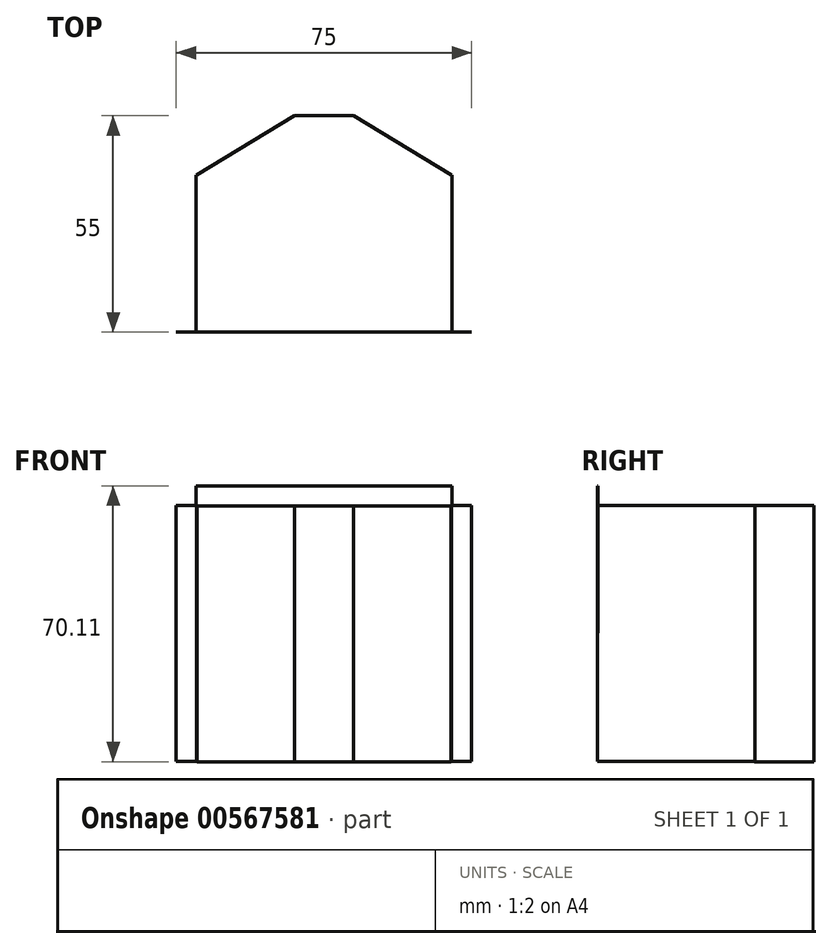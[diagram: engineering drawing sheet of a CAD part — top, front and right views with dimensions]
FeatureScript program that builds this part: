
annotation { "Feature Type Name" : "Feature", "Feature Type Description" : "" }
export const myFeature = defineFeature(function(context is Context, id is Id, definition is map)
    precondition{}
    {
        {
            var Q0;
            Q0=qCreatedBy(makeId("Front.planeOp"),FACE);
            var sketch = newSketch(context, id + "F0", { "sketchPlane" : qUnion([Q0])});
            skLineSegment(sketch, "E0", {"start": v(0, 0) * mm, "end": v(-65, 0) * mm});
            skLineSegment(sketch, "E1", {"start": v(-65, 0) * mm, "end": v(-65, -65) * mm});
            skLineSegment(sketch, "E2", {"start": v(-65, -65) * mm, "end": v(-64.89, -65) * mm});
            skLineSegment(sketch, "E3", {"start": v(-64.89, -65) * mm, "end": v(-64.89, -0.11) * mm});
            skLineSegment(sketch, "E4", {"start": v(-64.89, -0.1) * mm, "end": v(-0.11, -0.1) * mm});
            skLineSegment(sketch, "E5", {"start": v(-0.11, -0.1) * mm, "end": v(-0.1, -65) * mm});
            skLineSegment(sketch, "E6", {"start": v(-0.1, -65) * mm, "end": v(0, -65) * mm});
            skLineSegment(sketch, "E7", {"start": v(0, -65) * mm, "end": v(0, 0) * mm});
            skSolve(sketch);
        }
        {
            var Q0;
            Q0=makeQuery(id+"F0.imprint","IMPRINT",FACE,{"disambiguationData":[TD([[makeQuery(id+"F0.imprint","IMPRINT",EDGE,{"derivedFrom":sQuery(id+"F0.wireOp",EDGE,"E0")}),1.0]])]});
            extrude(context, id + "F1", {"entities" : qUnion([Q0]), "depth" : 35 * mm, "offsetDistance" : 25 * mm});
        }
        {
            var Q0;
            Q0=makeQuery(id+"F1.opExtrude","SWEPT_FACE",FACE,{"disambiguationData":[OSD([sQuery(id+"F0.wireOp",EDGE,"E1")])]});
            var sketch = newSketch(context, id + "F2", { "sketchPlane" : qUnion([Q0])});
            skLineSegment(sketch, "E8", {"start": v(34.9, 0) * mm, "end": v(34.9, -65) * mm});
            skSolve(sketch);
        }
        {
            var Q0;
            {var subQ0=sQuery(id+"F2.wireOp",EDGE,"E8");Q0=makeQuery(id+"F2.imprint","IMPRINT",FACE,{"disambiguationData":[TD([[makeQuery(id+"F2.imprint","IMPRINT",EDGE,{"derivedFrom":subQ0}),1.0]])]});}
            extrude(context, id + "F3", {"entities" : qUnion([Q0]), "operationType" : NewBodyOperationType.ADD, "depth" : 5 * mm, "offsetDistance" : 25 * mm});
        }
        {
            var Q0;
            {var subQ0=sQuery(id+"F0.wireOp",EDGE,"E0");Q0=makeQuery(id+"F3.boolean.opBoolean","MERGE",FACE,{"derivedFrom":[makeQuery(id+"Fdze2Mgvsd4NKJJ_1.boolean.opBoolean","MERGE",FACE,{"derivedFrom":[makeQuery(id+"F1.opExtrude","SWEPT_FACE",FACE,{"disambiguationData":[OSD([subQ0])]}),makeQuery(id+"Fdze2Mgvsd4NKJJ_1.opExtrude","SWEPT_FACE",FACE,{"disambiguationData":[OSD([sQuery(id+"FzqWdQqcZOJAViu_1.wireOp",EDGE,"lwhyzzlY-dMcn-4o8W-08A6-9XrshBXt5lzN.bottom")])]})]}),makeQuery(id+"F3.opExtrude","SWEPT_FACE",FACE,{"disambiguationData":[OSD([subQ0,sQuery(id+"F0.wireOp",EDGE,"E1")])]})]});}
            var sketch = newSketch(context, id + "F4", { "sketchPlane" : qUnion([Q0])});
            skLineSegment(sketch, "E9", {"start": v(-65, -34.9) * mm, "end": v(0, -35) * mm});
            skLineSegment(sketch, "E10", {"start": v(-65, -34.9) * mm, "end": v(-65, -35) * mm});
            skSolve(sketch);
        }
        {
            var Q0;
            {var subQ0=sQuery(id+"F4.wireOp",EDGE,"E9");Q0=makeQuery(id+"F4.imprint","IMPRINT",FACE,{"disambiguationData":[TD([[makeQuery(id+"F4.imprint","IMPRINT",EDGE,{"derivedFrom":subQ0}),-1.0]])]});}
            extrude(context, id + "F5", {"entities" : qUnion([Q0]), "operationType" : NewBodyOperationType.ADD, "depth" : 5 * mm, "offsetDistance" : 25 * mm});
        }
        {
            var Q0;
            Q0=makeQuery(id+"Fdze2Mgvsd4NKJJ_1.boolean.opBoolean","MERGE",FACE,{"derivedFrom":[makeQuery(id+"F1.opExtrude","SWEPT_FACE",FACE,{"disambiguationData":[OSD([sQuery(id+"F0.wireOp",EDGE,"E7")])]}),makeQuery(id+"Fdze2Mgvsd4NKJJ_1.opExtrude","SWEPT_FACE",FACE,{"disambiguationData":[OSD([sQuery(id+"FzqWdQqcZOJAViu_1.wireOp",EDGE,"lwhyzzlY-dMcn-4o8W-08A6-9XrshBXt5lzN.right")])]})]});
            var sketch = newSketch(context, id + "F6", { "sketchPlane" : qUnion([Q0])});
            skLineSegment(sketch, "E11", {"start": v(-34.89, 0) * mm, "end": v(-35, -65) * mm});
            skSolve(sketch);
        }
        {
            var Q0;
            {var subQ0=sQuery(id+"F6.wireOp",EDGE,"E11");Q0=makeQuery(id+"F6.imprint","IMPRINT",FACE,{"disambiguationData":[TD([[makeQuery(id+"F6.imprint","IMPRINT",EDGE,{"derivedFrom":subQ0}),-1.0]])]});}
            extrude(context, id + "F7", {"entities" : qUnion([Q0]), "operationType" : NewBodyOperationType.ADD, "depth" : 5 * mm, "offsetDistance" : 25 * mm});
        }
        {
            var Q0;
            Q0=makeQuery(id+"F1.opExtrude","CAP_FACE",FACE,{"disambiguationData":[OSD([sQuery(id+"F0.wireOp",EDGE,"E0"),sQuery(id+"F0.wireOp",EDGE,"E1"),sQuery(id+"F0.wireOp",EDGE,"E2"),sQuery(id+"F0.wireOp",EDGE,"E3"),sQuery(id+"F0.wireOp",EDGE,"E4"),sQuery(id+"F0.wireOp",EDGE,"E5"),sQuery(id+"F0.wireOp",EDGE,"E6"),sQuery(id+"F0.wireOp",EDGE,"E7")])],"isStart":true});
            extrude(context, id + "F8", {"entities" : qUnion([Q0]), "operationType" : NewBodyOperationType.ADD, "depth" : 20 * mm, "offsetDistance" : 25 * mm});
        }
        {
            var Q0;
            {var subQ0=sQuery(id+"F0.wireOp",EDGE,"E0");var subQ1=sQuery(id+"F0.wireOp",EDGE,"E7");var subQ2=sQuery(id+"F0.wireOp",EDGE,"E1");var subQ3=makeQuery(id+"F3.opExtrude","SWEPT_FACE",FACE,{"disambiguationData":[OSD([subQ0,subQ2])]});var subQ4=makeQuery(id+"F1.opExtrude","SWEPT_FACE",FACE,{"disambiguationData":[OSD([subQ0])]});Q0=makeQuery(id+"F8.boolean.opBoolean","MERGE",FACE,{"derivedFrom":[makeQuery(id+"F7.boolean.opBoolean","MERGE",FACE,{"derivedFrom":[makeQuery(id+"F5.boolean.opBoolean","SPLIT",FACE,{"disambiguationData":[TD([makeQuery(id+"F1.opExtrude","SWEPT_FACE",FACE,{"disambiguationData":[OSD([subQ1])]})])],"derivedFrom":makeQuery(id+"F3.boolean.opBoolean","MERGE",FACE,{"derivedFrom":[subQ4,subQ3]})}),makeQuery(id+"F7.opExtrude","SWEPT_FACE",FACE,{"disambiguationData":[OSD([subQ0,subQ1])]})]}),makeQuery(id+"F8.opExtrude","SWEPT_FACE",FACE,{"disambiguationData":[OSD([subQ0])]})]});}
            var sketch = newSketch(context, id + "F9", { "sketchPlane" : qUnion([Q0])});
            skLineSegment(sketch, "E12", {"start": v(-40, 20) * mm, "end": v(-25, 20) * mm});
            skLineSegment(sketch, "E13", {"start": v(-25, 20) * mm, "end": v(-0.1, 5) * mm});
            skLineSegment(sketch, "E14", {"start": v(-0.11, 5) * mm, "end": v(0, 5) * mm});
            skLineSegment(sketch, "E15", {"start": v(-40, 20) * mm, "end": v(-64.89, 5) * mm});
            skLineSegment(sketch, "E16", {"start": v(-64.89, 5) * mm, "end": v(-65, 5) * mm});
            skSolve(sketch);
        }
        {
            var Q0;
            {var subQ0=sQuery(id+"F9.wireOp",EDGE,"E15");Q0=makeQuery(id+"F9.imprint","IMPRINT",FACE,{"disambiguationData":[TD([[makeQuery(id+"F9.imprint","IMPRINT",EDGE,{"derivedFrom":subQ0}),-1.0]])]});}
            var Q1;
            {var subQ0=sQuery(id+"F9.wireOp",EDGE,"E13");Q1=makeQuery(id+"F9.imprint","IMPRINT",FACE,{"disambiguationData":[TD([[makeQuery(id+"F9.imprint","IMPRINT",EDGE,{"derivedFrom":subQ0}),1.0]])]});}
            extrude(context, id + "F10", {"entities" : qUnion([Q0, Q1]), "operationType" : NewBodyOperationType.REMOVE, "endBound" : BoundingType.THROUGH_ALL, "oppositeDirection" : true, "depth" : 25 * mm, "offsetDistance" : 25 * mm});
        }
        {
            var Q0;
            {var subQ0=sQuery(id+"F0.wireOp",EDGE,"E4");Q0=makeQuery(id+"F8.boolean.opBoolean","MERGE",FACE,{"derivedFrom":[makeQuery(id+"F1.opExtrude","SWEPT_FACE",FACE,{"disambiguationData":[OSD([subQ0])]}),makeQuery(id+"F8.opExtrude","SWEPT_FACE",FACE,{"disambiguationData":[OSD([subQ0])]})]});}
            var sketch = newSketch(context, id + "F11", { "sketchPlane" : qUnion([Q0])});
            skLineSegment(sketch, "E17.0", {"start": v(-25.06, -19.9) * mm, "end": v(-25.03, -19.9) * mm});
            skLineSegment(sketch, "E17.1", {"start": v(-25.03, -19.9) * mm, "end": v(-25.03, -19.9) * mm});
            skLineSegment(sketch, "E18", {"start": v(-25.06, -19.9) * mm, "end": v(-25, -20) * mm});
            skLineSegment(sketch, "E19.0", {"start": v(-39.97, -19.89) * mm, "end": v(-64.75, -4.95) * mm});
            skLineSegment(sketch, "E19.1", {"start": v(-39.97, -19.9) * mm, "end": v(-25.03, -19.9) * mm});
            skLineSegment(sketch, "E19.2", {"start": v(-25.03, -19.89) * mm, "end": v(-0.17, -4.9) * mm});
            skLineSegment(sketch, "E20", {"start": v(-0.15, -5.02) * mm, "end": v(-0.17, -4.9) * mm});
            skLineSegment(sketch, "E21", {"start": v(-64.75, -4.95) * mm, "end": v(-64.75, -5.08) * mm});
            skLineSegment(sketch, "E22", {"start": v(-64.75, -5.08) * mm, "end": v(-61.17, -7.25) * mm});
            skSolve(sketch);
        }
        {
            var Q0;
            Q0=makeQuery(id+"F11.imprint","IMPRINT",FACE,{"disambiguationData":[TD([[makeQuery(id+"F11.imprint","IMPRINT",EDGE,{"derivedFrom":sQuery(id+"F11.wireOp",EDGE,"E17.0")}),-1.0]])]});
            var Q1;
            Q1=makeQuery(id+"F11.imprint","IMPRINT",FACE,{"disambiguationData":[TD([[makeQuery(id+"F11.imprint","IMPRINT",EDGE,{"derivedFrom":sQuery(id+"F11.wireOp",EDGE,"E17.0")}),1.0]])]});
            extrude(context, id + "F12", {"entities" : qUnion([Q0, Q1]), "operationType" : NewBodyOperationType.ADD, "depth" : 65 * mm, "offsetDistance" : 25 * mm});
        }
    });
